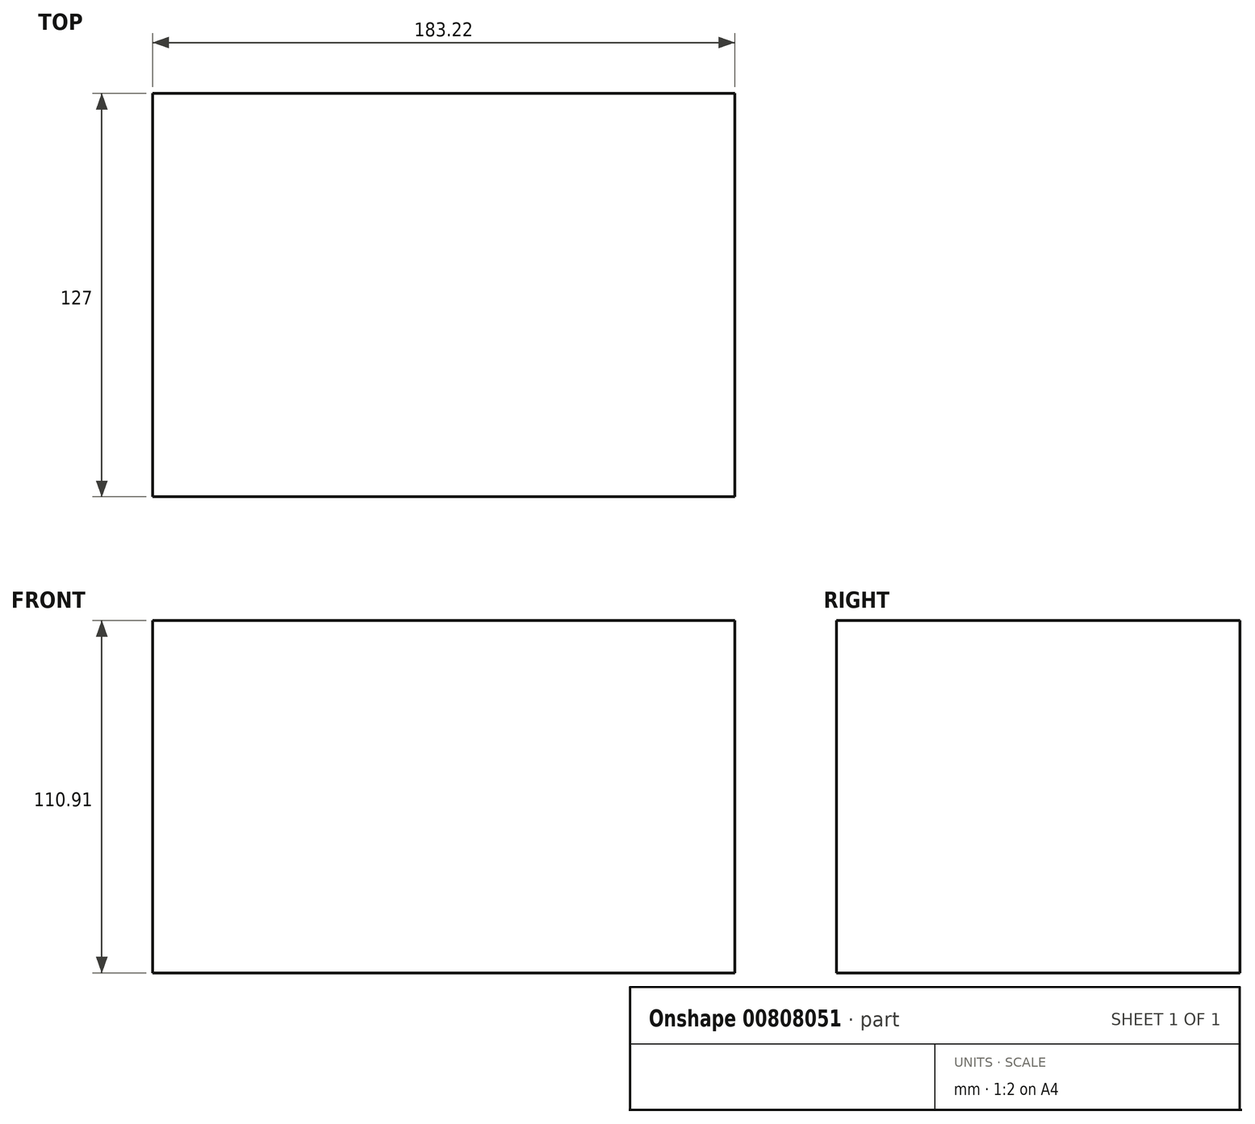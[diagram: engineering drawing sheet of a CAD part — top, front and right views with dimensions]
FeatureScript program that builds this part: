
annotation { "Feature Type Name" : "Feature", "Feature Type Description" : "" }
export const myFeature = defineFeature(function(context is Context, id is Id, definition is map)
    precondition{}
    {
        {
            var Q0;
            Q0=qCreatedBy(makeId("Front.planeOp"),FACE);
            var sketch = newSketch(context, id + "F0", { "sketchPlane" : qUnion([Q0])});
            skLineSegment(sketch, "E0.bottom", {"start": v(0, 0) * mm, "end": v(183.22, 0) * mm});
            skLineSegment(sketch, "E0.top", {"start": v(0, 110.9) * mm, "end": v(183.22, 110.9) * mm});
            skLineSegment(sketch, "E0.left", {"start": v(0, 0) * mm, "end": v(0, 110.9) * mm});
            skLineSegment(sketch, "E0.right", {"start": v(183.22, 0) * mm, "end": v(183.22, 110.9) * mm});
            skSolve(sketch);
        }
        {
            var Q0;
            Q0=makeQuery(id+"F0.imprint","IMPRINT",FACE,{"disambiguationData":[TD([[makeQuery(id+"F0.imprint","IMPRINT",EDGE,{"derivedFrom":sQuery(id+"F0.wireOp",EDGE,"E0.bottom")}),1.0]])]});
            extrude(context, id + "F1", {"entities" : qUnion([Q0]), "depth" : 127 * mm, "offsetDistance" : 25.4 * mm});
        }
    });
